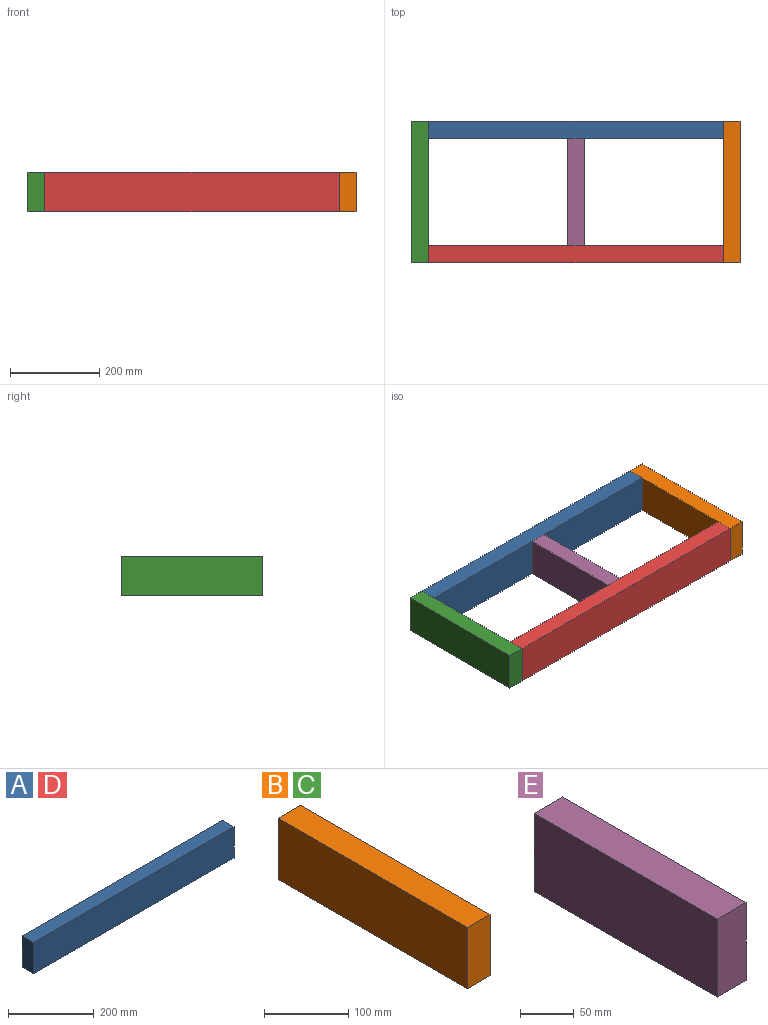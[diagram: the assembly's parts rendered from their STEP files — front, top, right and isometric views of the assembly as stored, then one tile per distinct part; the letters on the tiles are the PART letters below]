
ASSEMBLY  parts=5 mates=4
PART A: 6 faces, bbox 660.4x38.1x88.9 mm
  f0: plane 660.4x38.1mm, normal (0,0,1), area 25161.2mm2, adj f1,f3,f4,f5
  f1: plane 88.9x38.1mm, normal (-1,0,0), area 3387.1mm2, adj f0,f2,f4,f5
  f2: plane 660.4x38.1mm, normal (0,0,-1), area 25161.2mm2, adj f1,f3,f4,f5
  f3: plane 88.9x38.1mm, normal (1,0,0), area 3387.1mm2, adj f0,f2,f4,f5
  f4: plane 660.4x88.9mm, normal (0,-1,0), area 58709.6mm2, adj f0,f1,f2,f3
  f5: plane 660.4x88.9mm, normal (0,1,0), area 58709.6mm2, adj f0,f1,f2,f3
PART B: 6 faces, bbox 38.1x317.5x88.9 mm
  f0: plane 317.5x38.1mm, normal (0,0,1), area 12096.7mm2, adj f1,f3,f4,f5
  f1: plane 88.9x38.1mm, normal (0,-1,0), area 3387.1mm2, adj f0,f2,f4,f5
  f2: plane 317.5x38.1mm, normal (0,0,-1), area 12096.7mm2, adj f1,f3,f4,f5
  f3: plane 88.9x38.1mm, normal (0,1,0), area 3387.1mm2, adj f0,f2,f4,f5
  f4: plane 317.5x88.9mm, normal (1,0,0), area 28225.8mm2, adj f0,f1,f2,f3
  f5: plane 317.5x88.9mm, normal (-1,0,0), area 28225.8mm2, adj f0,f1,f2,f3
PART C: same geometry as B
PART D: same geometry as A
PART E: 6 faces, bbox 38.1x241.3x88.9 mm
  f0: plane 241.3x38.1mm, normal (0,0,1), area 9193.5mm2, adj f1,f3,f4,f5
  f1: plane 88.9x38.1mm, normal (0,-1,0), area 3387.1mm2, adj f0,f2,f4,f5
  f2: plane 241.3x38.1mm, normal (0,0,-1), area 9193.5mm2, adj f1,f3,f4,f5
  f3: plane 88.9x38.1mm, normal (0,1,0), area 3387.1mm2, adj f0,f2,f4,f5
  f4: plane 241.3x88.9mm, normal (1,0,0), area 21451.6mm2, adj f0,f1,f2,f3
  f5: plane 241.3x88.9mm, normal (-1,0,0), area 21451.6mm2, adj f0,f1,f2,f3
PLACE A t=(-47.51,179.62,81.76)mm
PLACE B t=(282.69,20.87,81.76)mm
PLACE C t=(-415.81,20.87,81.76)mm
PLACE D t=(-47.51,-99.78,81.76)mm
PLACE E t=(-66.56,20.87,77.94)mm
MATE fastened C.f4 <-> A.f1  axis (1,0,0) through (-377.71,179.62,126.21)mm
MATE fastened E.f3 <-> A.f4  axis (0,1,0) through (-47.51,141.52,126.21)mm
MATE fastened D.f1 <-> C.f4  axis (1,0,0) through (-377.71,-137.88,126.21)mm
MATE fastened B.f5 <-> D.f3  axis (-1,0,0) through (282.69,-137.88,126.21)mm
